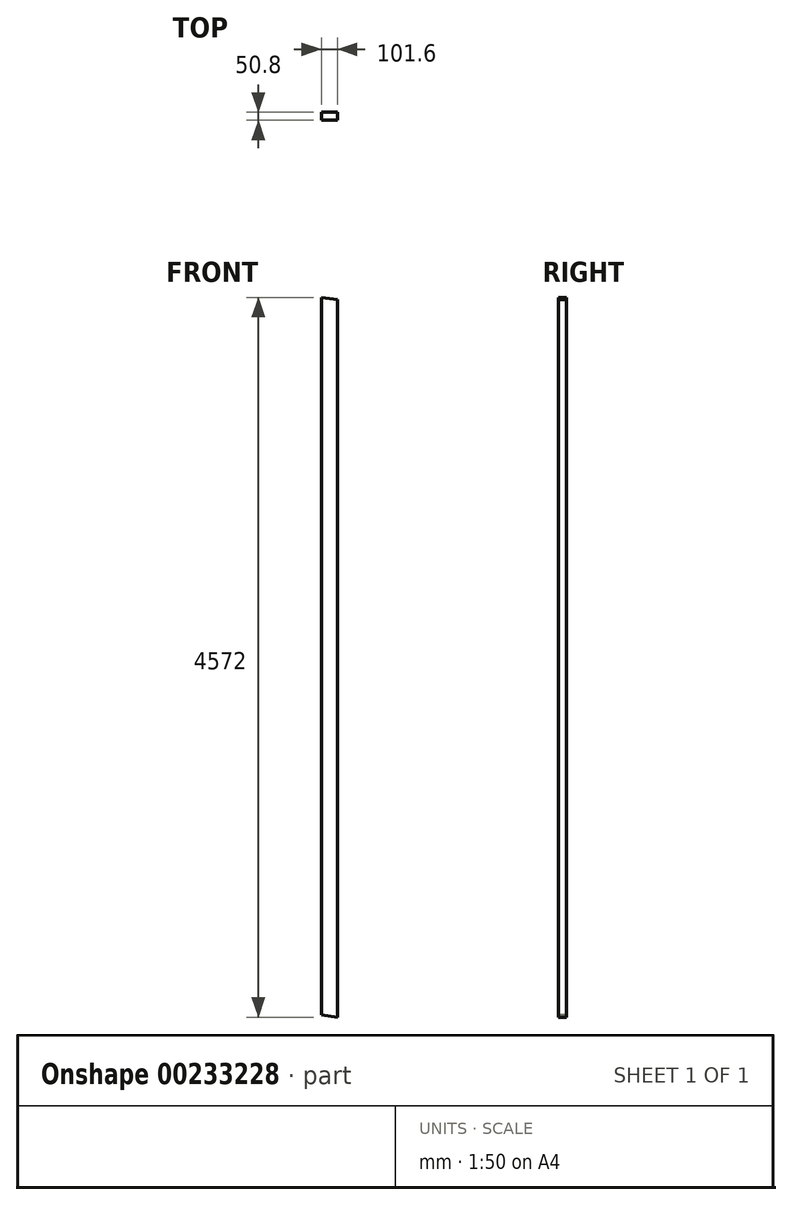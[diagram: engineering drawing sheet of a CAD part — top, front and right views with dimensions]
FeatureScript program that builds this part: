
annotation { "Feature Type Name" : "Feature", "Feature Type Description" : "" }
export const myFeature = defineFeature(function(context is Context, id is Id, definition is map)
    precondition{}
    {
        {
            var Q0;
            Q0=qCreatedBy(makeId("Front.planeOp"),FACE);
            var sketch = newSketch(context, id + "F0", { "sketchPlane" : qUnion([Q0])});
            skLineSegment(sketch, "E0.bottom", {"start": v(57.51, 4450.6) * mm, "end": v(-44.09, 4450.6) * mm});
            skLineSegment(sketch, "E0.top", {"start": v(57.51, -121.4) * mm, "end": v(-44.09, -121.4) * mm});
            skLineSegment(sketch, "E0.left", {"start": v(57.51, 4450.6) * mm, "end": v(57.51, -121.4) * mm});
            skLineSegment(sketch, "E0.right", {"start": v(-44.09, 4450.6) * mm, "end": v(-44.09, -121.4) * mm});
            skSolve(sketch);
        }
        {
            var Q0;
            Q0=qSketchRegion(id+"F0",true);
            extrude(context, id + "F1", {"entities" : qUnion([Q0]), "depth" : 50.8 * mm});
        }
        {
            var Q0;
            Q0=makeQuery(id+"F1.opExtrude","CAP_FACE",FACE,{"disambiguationData":[OSD([sQuery(id+"F0.wireOp",EDGE,"E0.bottom"),sQuery(id+"F0.wireOp",EDGE,"E0.top"),sQuery(id+"F0.wireOp",EDGE,"E0.left"),sQuery(id+"F0.wireOp",EDGE,"E0.right")])],"isStart":false});
            var sketch = newSketch(context, id + "F2", { "sketchPlane" : qUnion([Q0])});
            skLineSegment(sketch, "E1", {"start": v(-44.09, 4450.6) * mm, "end": v(57.51, 4450.6) * mm});
            skLineSegment(sketch, "E2", {"start": v(57.51, 4450.6) * mm, "end": v(57.51, 4435.6) * mm});
            skLineSegment(sketch, "E3", {"start": v(57.51, 4435.6) * mm, "end": v(-44.09, 4450.6) * mm});
            skLineSegment(sketch, "E4", {"start": v(57.51, -121.4) * mm, "end": v(-44.09, -121.4) * mm});
            skLineSegment(sketch, "E5", {"start": v(-44.09, -121.4) * mm, "end": v(-44.09, -106.4) * mm});
            skLineSegment(sketch, "E6", {"start": v(-44.09, -106.4) * mm, "end": v(57.51, -121.4) * mm});
            skSolve(sketch);
        }
        {
            var Q0;
            Q0 = qSketchRegion(id + "F2", true);
            extrude(context, id + "F3", {"entities" : qUnion([Q0]), "operationType" : NewBodyOperationType.REMOVE, "oppositeDirection" : true, "depth" : 123.7 * mm});
        }
    });
